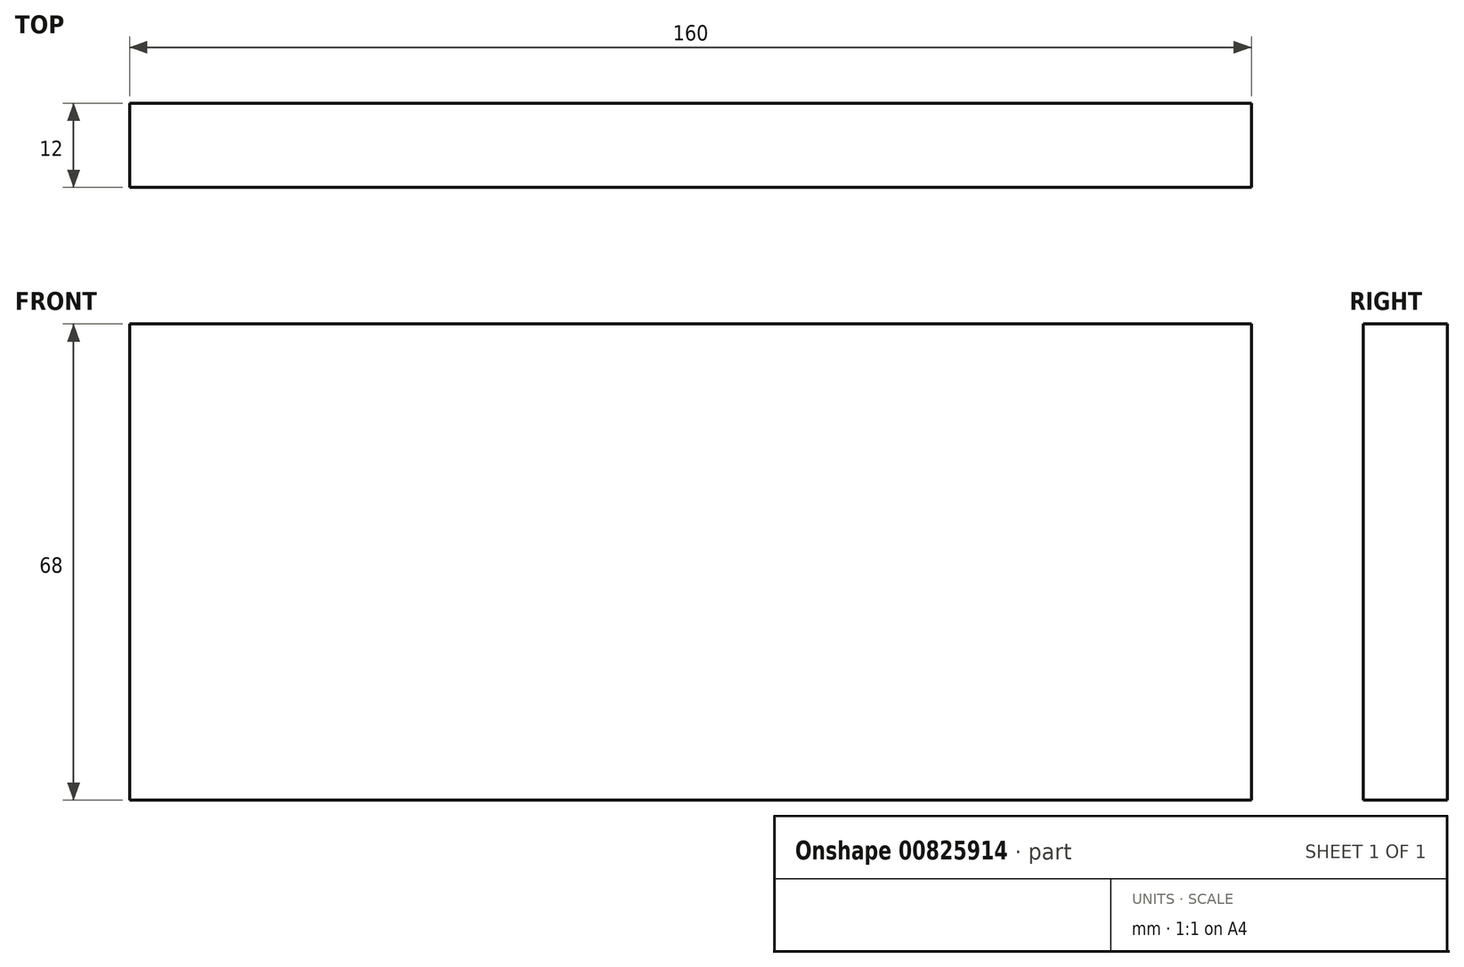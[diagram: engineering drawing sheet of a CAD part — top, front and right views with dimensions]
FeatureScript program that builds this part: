
annotation { "Feature Type Name" : "Feature", "Feature Type Description" : "" }
export const myFeature = defineFeature(function(context is Context, id is Id, definition is map)
    precondition{}
    {
        {
            var Q0;
            Q0=qCreatedBy(makeId("Right.planeOp"),FACE);
            var sketch = newSketch(context, id + "F0", { "sketchPlane" : qUnion([Q0])});
            skLineSegment(sketch, "E0.bottom", {"start": v(1.69, 0) * mm, "end": v(13.69, 0) * mm});
            skLineSegment(sketch, "E0.top", {"start": v(1.69, 68) * mm, "end": v(13.69, 68) * mm});
            skLineSegment(sketch, "E0.left", {"start": v(1.69, 0) * mm, "end": v(1.69, 68) * mm});
            skLineSegment(sketch, "E0.right", {"start": v(13.69, 0) * mm, "end": v(13.69, 68) * mm});
            skSolve(sketch);
        }
        {
            var Q0;
            Q0 = qSketchRegion(id + "F0", true);
            extrude(context, id + "F1", {"entities" : qUnion([Q0]), "depth" : 16 * mm, "offsetDistance" : 25 * mm});
        }
        {
            var Q0;
            Q0 = qSketchRegion(id + "F0", true);
            extrude(context, id + "F2", {"entities" : qUnion([Q0]), "operationType" : NewBodyOperationType.ADD, "depth" : 160 * mm, "offsetDistance" : 25 * mm});
        }
    });
